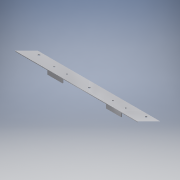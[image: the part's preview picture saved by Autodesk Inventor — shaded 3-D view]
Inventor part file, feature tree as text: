
AUTODESK INVENTOR PART (.ipt)
format: ipt  version: 2016 (Build 200138000, 138)  size: 194,560 bytes
history: native  units: in
note: dims shown in document units (in); Inventor stores cm internally (conversion verified against a paired STEP export)
features: extrude x5, sketch x5
ambient origin geometry x8: Origin, YZ Plane, XZ Plane, XY Plane, X Axis, Y Axis, Z Axis, Center Point
bodies: Solid1 (feature_tree)
feature tree (10):
  extrude  "Extrusion1"  Depth=2.0in
  extrude  "Extrusion2"  Depth=0.125in
  extrude  "Extrusion3"  Depth=15.0in
  extrude  "Extrusion4"  Depth=0.125in
  extrude  "Extrusion5"  Depth=2.25in
  sketch  "Sketch1"  dims[d0=30.0in d1=2.0in]
  sketch  "Sketch2"  dims[d2=0.125in d3=0.0in d4=0.375in]
  sketch  "Sketch3"  dims[d5=1.125in d6=15.0in]
  sketch  "Sketch4"  dims[d7=0.125in d8=0.0in d9=0.375in]
  sketch  "Sketch5"  dims[d10=1.5in d12=0.375in d13=1.5in d15=30.0in d16=0.875in d17=0.125in d18=0.0in d19=30.0in d20=0.875in d21=0.125in d22=0.0in d23=6.5in d24=1.25in d25=8.5in d26=3.0in d27=6.5in d28=1.25in d29=2.25in d30=0.0in d31=10.5in d32=10.5in d33=0.2656in d34=8.0in d35=1.0in d36=0.2656in d37=1.0in d38=10.5in d39=0.2656in d40=0.2656in d41=1.0in d42=1.0in d43=8.0in d44=10.5in]
